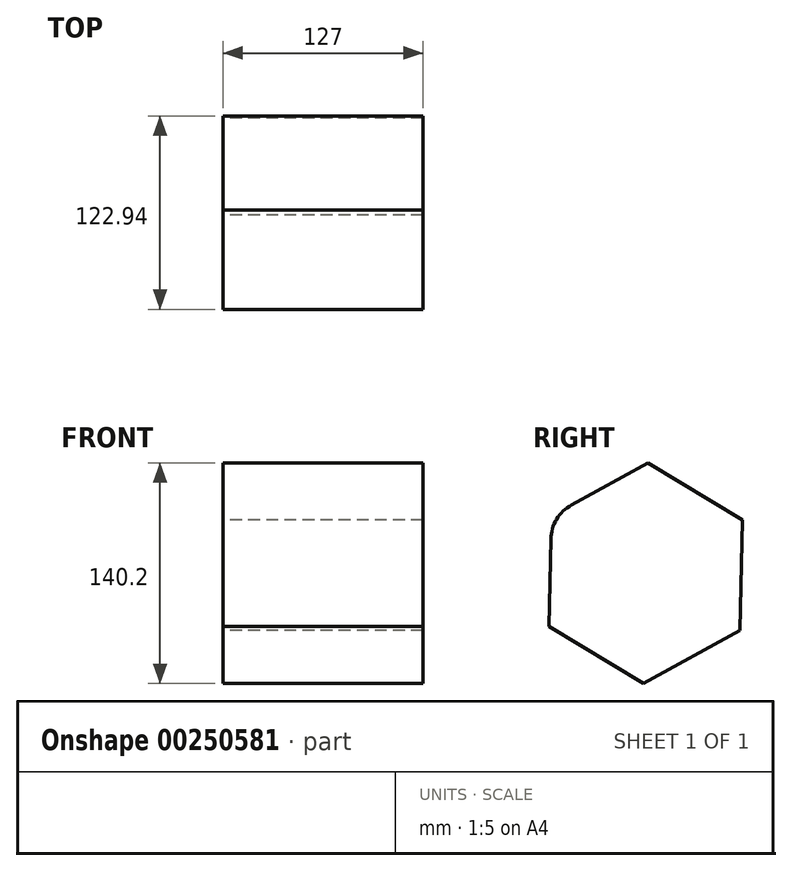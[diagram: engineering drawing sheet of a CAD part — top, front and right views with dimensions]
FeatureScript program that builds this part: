
annotation { "Feature Type Name" : "Feature", "Feature Type Description" : "" }
export const myFeature = defineFeature(function(context is Context, id is Id, definition is map)
    precondition{}
    {
        {
            var Q0;
            Q0=qCreatedBy(makeId("Right.planeOp"),FACE);
            var sketch = newSketch(context, id + "F0", { "sketchPlane" : qUnion([Q0])});
            skCircle(sketch, "E0.cCircle", {"center": v(0, 0) * mm, "radius": 60.72 * mm, "construction": true});
            skLineSegment(sketch, "E0.0", {"start": v(-1.53, -70.1) * mm, "end": v(-61.47, -33.73) * mm});
            skLineSegment(sketch, "E0.1", {"start": v(-61.47, -33.73) * mm, "end": v(-59.94, 36.37) * mm});
            skLineSegment(sketch, "E0.2", {"start": v(-59.94, 36.37) * mm, "end": v(1.53, 70.1) * mm});
            skLineSegment(sketch, "E0.3", {"start": v(1.53, 70.1) * mm, "end": v(61.47, 33.73) * mm});
            skLineSegment(sketch, "E0.4", {"start": v(61.47, 33.73) * mm, "end": v(59.94, -36.37) * mm});
            skLineSegment(sketch, "E0.5", {"start": v(59.94, -36.37) * mm, "end": v(-1.53, -70.1) * mm});
            skPoint(sketch, "E0.0.midPoint", {"position": v(-31.5, -51.91) * mm});
            skSolve(sketch);
        }
        {
            var Q0;
            Q0 = qSketchRegion(id + "F0", true);
            extrude(context, id + "F1", {"entities" : qUnion([Q0]), "endBound" : BoundingType.SYMMETRIC, "depth" : 127 * mm});
        }
        {
            var Q0;
            Q0=makeQuery(id+"F1.opExtrude","SWEPT_EDGE",EDGE,{"disambiguationData":[OSD([sQuery(id+"F0.wireOp",EDGE,"E0.1"),sQuery(id+"F0.wireOp",EDGE,"E0.2")])]});
            fillet(context, id + "F2", {"entities" : qUnion([Q0]), "radius" : 25.4 * mm, "tangentPropagation" : true, "allowEdgeOverflow" : false});
        }
    });
